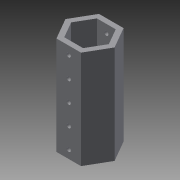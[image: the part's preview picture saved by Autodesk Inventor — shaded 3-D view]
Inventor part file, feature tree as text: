
AUTODESK INVENTOR PART (.ipt)
format: ipt  version: 2015 SP1 (Build 190203100, 203)  size: 112,640 bytes
history: native  units: mm
features: extrude x2, sketch x2, other x1, projected_geometry x1
ambient origin geometry x8: Origin, YZ Plane, XZ Plane, XY Plane, X Axis, Y Axis, Z Axis, Center Point
bodies: Body1 (feature_tree)
feature tree (6):
  other  "Sólido1"
  extrude  "Extrusión1"  Depth=12.0mm
  extrude  "Extrusión2"  Depth=24.0mm
  sketch  "Boceto1"  dims[d0=9.2mm d1=12.0mm]
  sketch  "Boceto2"  dims[d2=24.0mm d3=0.0mm d4=2.0mm d5=5.0mm d6=5.0mm d7=5.0mm d8=5.0mm d9=1.0mm d10=1.0mm d11=1.0mm d12=1.0mm d13=1.0mm d14=24.0mm d15=0.0mm]
  projected_geometry  "Contorno proyectado1"
